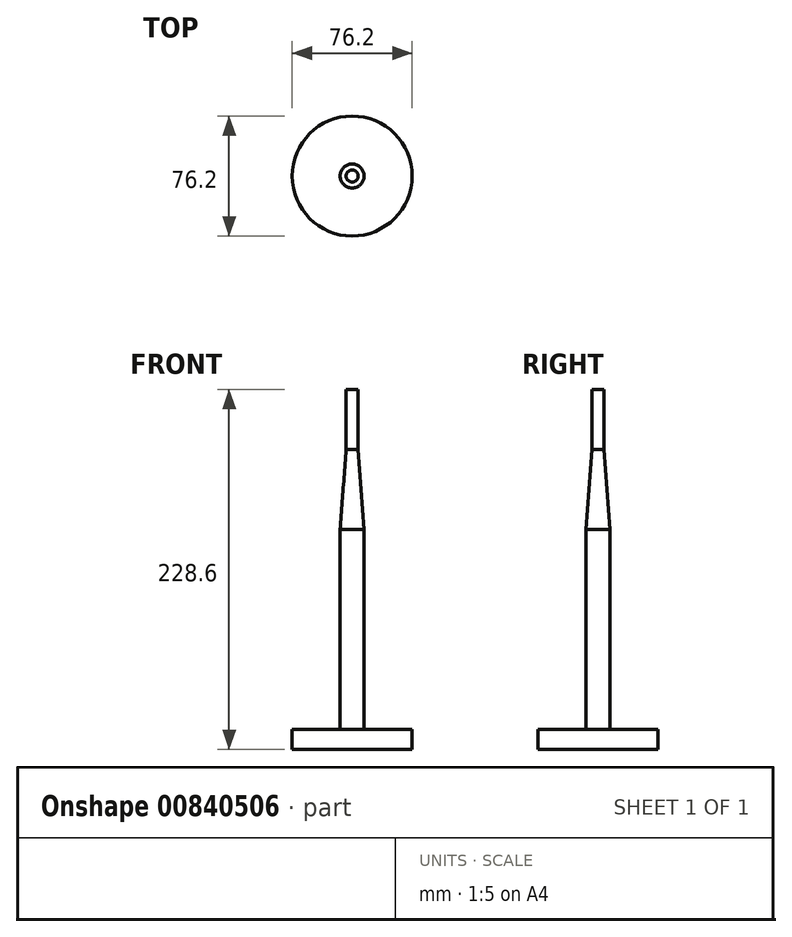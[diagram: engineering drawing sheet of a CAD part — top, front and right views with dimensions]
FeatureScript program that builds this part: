
annotation { "Feature Type Name" : "Feature", "Feature Type Description" : "" }
export const myFeature = defineFeature(function(context is Context, id is Id, definition is map)
    precondition{}
    {
        {
            var Q0;
            Q0=qCreatedBy(makeId("Top.planeOp"),FACE);
            var sketch = newSketch(context, id + "F0", { "sketchPlane" : qUnion([Q0])});
            skCircle(sketch, "E0", {"center": v(0, 0) * mm, "radius": 38.1 * mm});
            skSolve(sketch);
        }
        {
            var Q0;
            Q0=makeQuery(id+"F0.imprint","IMPRINT",FACE,{"disambiguationData":[TD([[makeQuery(id+"F0.imprint","IMPRINT",EDGE,{"derivedFrom":sQuery(id+"F0.wireOp",EDGE,"E0")}),1.0]])]});
            extrude(context, id + "F1", {"entities" : qUnion([Q0]), "depth" : 12.7 * mm, "offsetDistance" : 25.4 * mm});
        }
        {
            var Q0;
            Q0=makeQuery(id+"F1.opExtrude","CAP_FACE",FACE,{"disambiguationData":[OSD([sQuery(id+"F0.wireOp",EDGE,"E0")])],"isStart":false});
            var sketch = newSketch(context, id + "F2", { "sketchPlane" : qUnion([Q0])});
            skCircle(sketch, "E1", {"center": v(0, 0) * mm, "radius": 7.62 * mm});
            skSolve(sketch);
        }
        {
            var Q0;
            Q0=makeQuery(id+"F2.imprint","IMPRINT",FACE,{"disambiguationData":[TD([[makeQuery(id+"F2.imprint","IMPRINT",EDGE,{"derivedFrom":sQuery(id+"F2.wireOp",EDGE,"E1")}),1.0]])]});
            var Q1;
            Q1 = qSketchRegion(id + "F4", true);
            extrude(context, id + "F3", {"entities" : qUnion([Q0, Q1]), "operationType" : NewBodyOperationType.ADD, "depth" : 127 * mm, "offsetDistance" : 25.4 * mm});
        }
        {
            var Q0;
            Q0=qCreatedBy(makeId("Right.planeOp"),FACE);
            var sketch = newSketch(context, id + "F4", { "sketchPlane" : qUnion([Q0])});
            skLineSegment(sketch, "E2", {"start": v(0, 139.7) * mm, "end": v(0, 190.5) * mm});
            skLineSegment(sketch, "E3", {"start": v(0, 190.5) * mm, "end": v(3.81, 190.5) * mm});
            skLineSegment(sketch, "E4", {"start": v(0, 139.7) * mm, "end": v(7.62, 139.7) * mm});
            skLineSegment(sketch, "E5", {"start": v(7.62, 139.7) * mm, "end": v(3.81, 190.5) * mm});
            skSolve(sketch);
        }
        {
            var Q0;
            Q0=makeQuery(id+"F4.imprint","IMPRINT",FACE,{"disambiguationData":[TD([[makeQuery(id+"F4.imprint","IMPRINT",EDGE,{"derivedFrom":sQuery(id+"F4.wireOp",EDGE,"E2")}),-1.0]])]});
            var Q1;
            Q1=sQuery(id+"F4.wireOp",EDGE,"E2");
            revolve(context, id + "F5", {"operationType" : NewBodyOperationType.ADD, "surfaceOperationType" : NewSurfaceOperationType.NEW, "entities" : qUnion([Q0]), "axis" : qUnion([Q1]), "revolveType" : RevolveType.FULL});
        }
        {
            var Q0;
            Q0=makeQuery(id+"F5.opRevolve","SWEPT_FACE",FACE,{"disambiguationData":[OSD([sQuery(id+"F4.wireOp",EDGE,"E3")])]});
            extrude(context, id + "F6", {"entities" : qUnion([Q0]), "operationType" : NewBodyOperationType.ADD, "depth" : 38.1 * mm, "offsetDistance" : 25.4 * mm});
        }
    });
